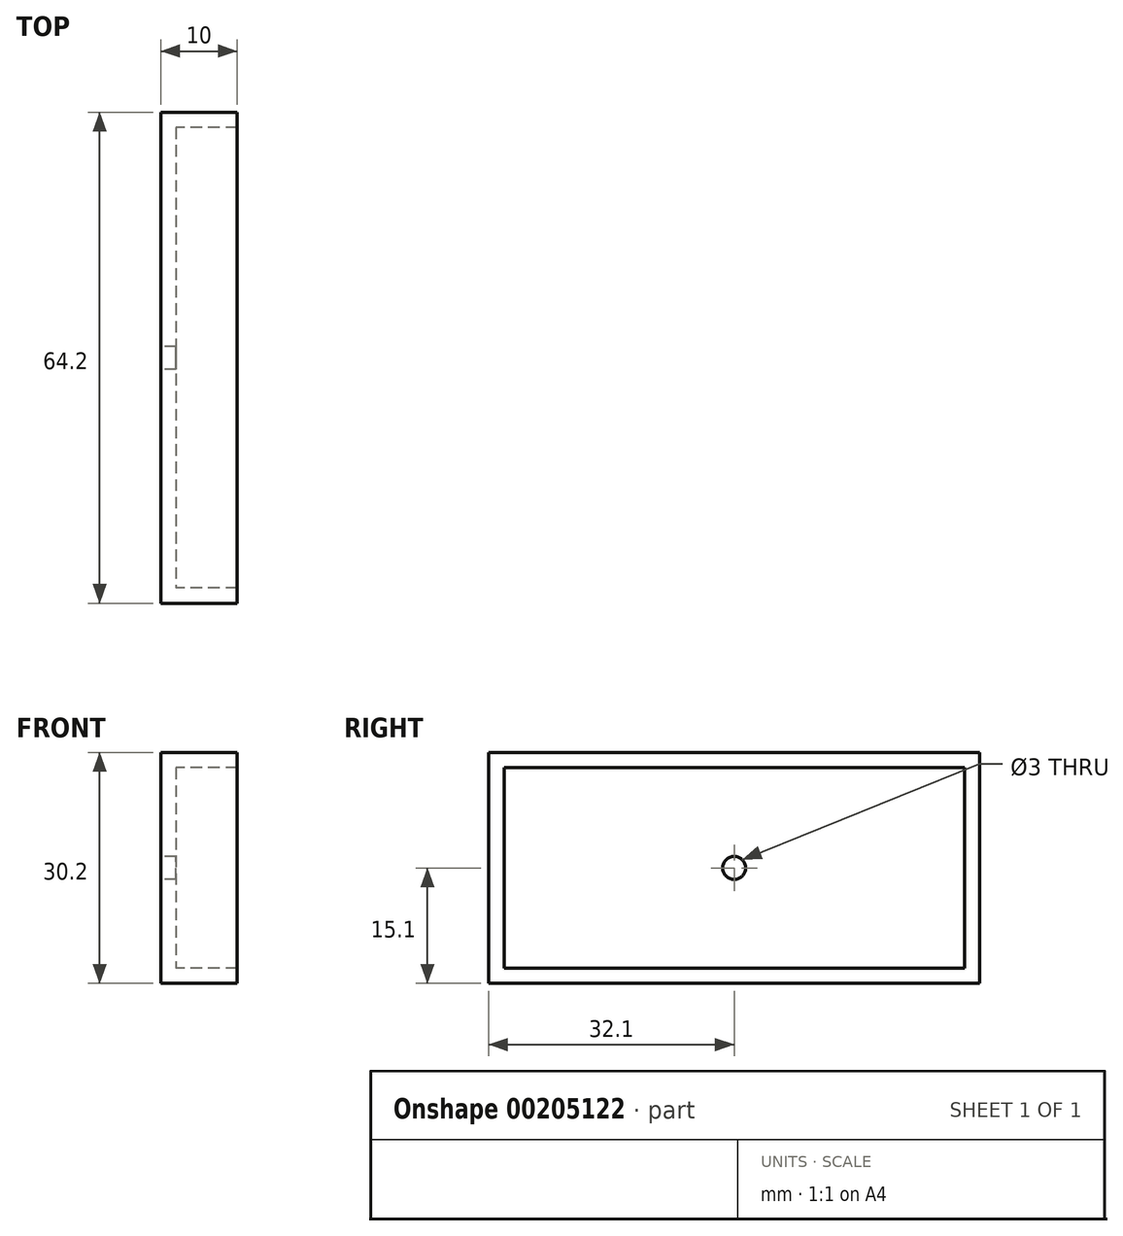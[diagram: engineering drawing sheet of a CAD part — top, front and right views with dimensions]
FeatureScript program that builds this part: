
annotation { "Feature Type Name" : "Feature", "Feature Type Description" : "" }
export const myFeature = defineFeature(function(context is Context, id is Id, definition is map)
    precondition{}
    {
        {
            var Q0;
            Q0=qCreatedBy(makeId("Right.planeOp"),FACE);
            var sketch = newSketch(context, id + "F0", { "sketchPlane" : qUnion([Q0])});
            skLineSegment(sketch, "E0", {"start": v(0, 0) * mm, "end": v(-60.2, 0) * mm});
            skLineSegment(sketch, "E1", {"start": v(-60.2, 0) * mm, "end": v(-60.2, 26.2) * mm});
            skLineSegment(sketch, "E2", {"start": v(-60.2, 26.2) * mm, "end": v(0, 26.2) * mm});
            skLineSegment(sketch, "E3", {"start": v(0, 26.2) * mm, "end": v(0, 0) * mm});
            skLineSegment(sketch, "E4", {"start": v(-60.2, 0) * mm, "end": v(-62.2, 0) * mm});
            skLineSegment(sketch, "E5", {"start": v(-62.2, 0) * mm, "end": v(-62.2, 28.2) * mm});
            skLineSegment(sketch, "E6", {"start": v(-30.1, 26.2) * mm, "end": v(-30.1, 28.2) * mm});
            skLineSegment(sketch, "E7", {"start": v(-30.1, 28.2) * mm, "end": v(-62.2, 28.2) * mm});
            skLineSegment(sketch, "E8.MirrorCS", {"start": v(-30.1, 28.2) * mm, "end": v(2, 28.2) * mm});
            skLineSegment(sketch, "E9.MirrorCS", {"start": v(2, 0) * mm, "end": v(2, 28.2) * mm});
            skLineSegment(sketch, "E10.MirrorCS", {"start": v(0, 0) * mm, "end": v(2, 0) * mm});
            skLineSegment(sketch, "E11", {"start": v(-62.2, 0) * mm, "end": v(-62.2, -2) * mm});
            skLineSegment(sketch, "E12", {"start": v(-62.2, -2) * mm, "end": v(2, -2) * mm});
            skLineSegment(sketch, "E13", {"start": v(2, -2) * mm, "end": v(2, 0) * mm});
            skLineSegment(sketch, "E14", {"start": v(-30.1, 0) * mm, "end": v(-30.1, 26.2) * mm});
            skLineSegment(sketch, "E15", {"start": v(-30.1, 13.1) * mm, "end": v(-34.08, 13.1) * mm});
            skCircle(sketch, "E16", {"center": v(-30.1, 13.1) * mm, "radius": 1.5 * mm});
            skSolve(sketch);
        }
        {
            var Q0;
            Q0 = qSketchRegion(id + "F0", true);
            var Q1;
            {var subQ6=sQuery(id+"F0.wireOp",EDGE,"E1");Q1=makeQuery(id+"F0.imprint","IMPRINT",FACE,{"disambiguationData":[TD([[makeQuery(id+"F0.imprint","IMPRINT",EDGE,{"derivedFrom":subQ6}),-1.0]])]});}
            var Q2;
            {var subQ0=sQuery(id+"F0.wireOp",EDGE,"E3");Q2=makeQuery(id+"F0.imprint","IMPRINT",FACE,{"disambiguationData":[TD([[makeQuery(id+"F0.imprint","IMPRINT",EDGE,{"derivedFrom":subQ0}),-1.0]])]});}
            extrude(context, id + "F1", {"entities" : qUnion([Q0, Q1, Q2]), "depth" : 2 * mm});
        }
        {
            var Q0;
            {var subQ1=sQuery(id+"F0.wireOp",EDGE,"E3");Q0=makeQuery(id+"F0.imprint","IMPRINT",FACE,{"disambiguationData":[TD([[makeQuery(id+"F0.imprint","IMPRINT",EDGE,{"derivedFrom":subQ1}),1.0]])]});}
            var Q1;
            {var subQ1=sQuery(id+"F0.wireOp",EDGE,"E4");Q1=makeQuery(id+"F0.imprint","IMPRINT",FACE,{"disambiguationData":[TD([[makeQuery(id+"F0.imprint","IMPRINT",EDGE,{"derivedFrom":subQ1}),1.0]])]});}
            var Q2;
            {var subQ1=sQuery(id+"F0.wireOp",EDGE,"E1");Q2=makeQuery(id+"F0.imprint","IMPRINT",FACE,{"disambiguationData":[TD([[makeQuery(id+"F0.imprint","IMPRINT",EDGE,{"derivedFrom":subQ1}),1.0]])]});}
            extrude(context, id + "F2", {"entities" : qUnion([Q0, Q1, Q2]), "operationType" : NewBodyOperationType.ADD, "depth" : 10 * mm});
        }
    });
